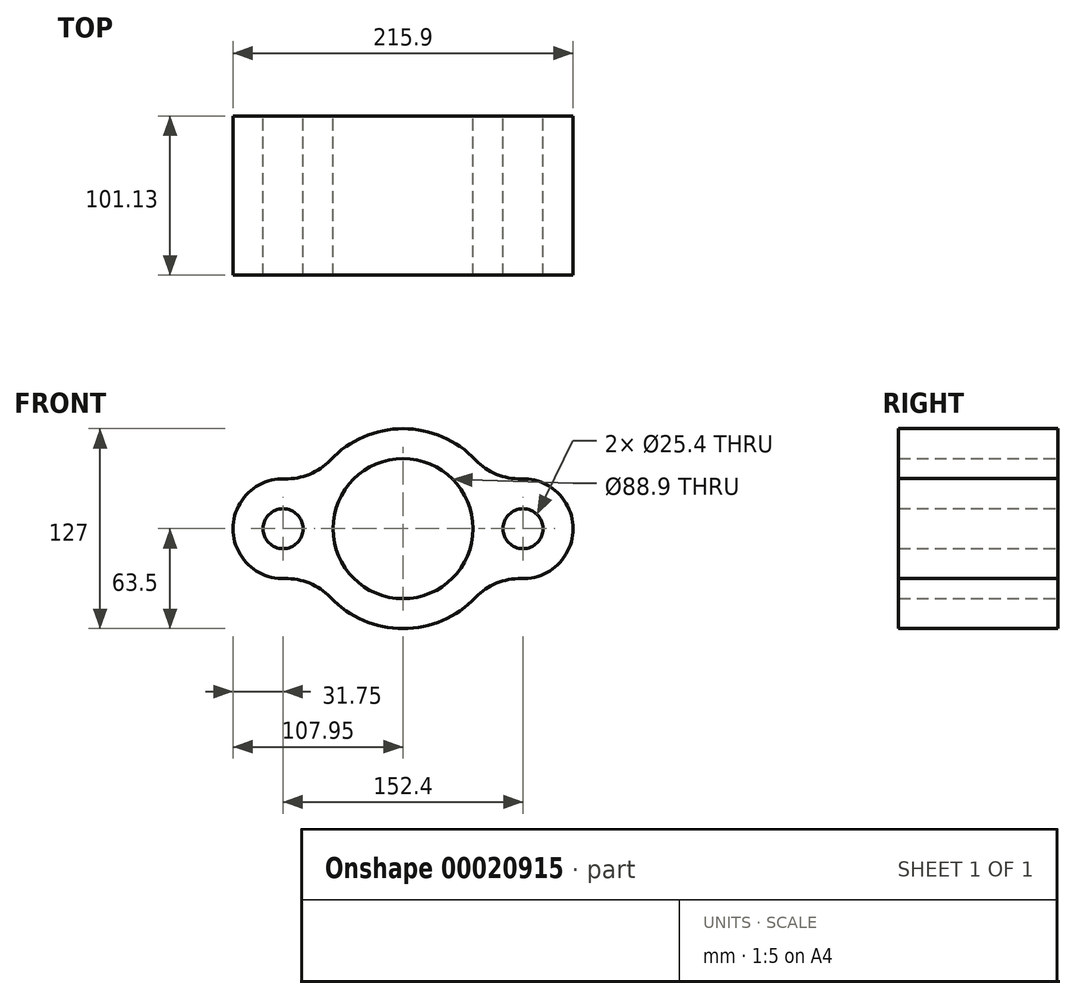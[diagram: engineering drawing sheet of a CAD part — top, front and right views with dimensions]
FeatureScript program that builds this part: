
annotation { "Feature Type Name" : "Feature", "Feature Type Description" : "" }
export const myFeature = defineFeature(function(context is Context, id is Id, definition is map)
    precondition{}
    {
        {
            var Q0;
            Q0=qCreatedBy(makeId("Front.planeOp"),FACE);
            var sketch = newSketch(context, id + "F0", { "sketchPlane" : qUnion([Q0])});
            skCircle(sketch, "E0", {"center": v(0, 0) * mm, "radius": 44.45 * mm});
            skCircle(sketch, "E1", {"center": v(-76.2, 0) * mm, "radius": 12.7 * mm});
            skCircle(sketch, "E2", {"center": v(76.2, 0) * mm, "radius": 12.7 * mm});
            skArc(sketch, "E3", {"start": v(46.14, 43.63) * mm, "mid": v(0, 63.5) * mm, "end": v(-46.14, 43.63) * mm});
            skArc(sketch, "E4", {"start": v(-75.12, 31.73) * mm, "mid": v(-107.95, 0) * mm, "end": v(-75.12, -31.73) * mm});
            skArc(sketch, "E5", {"start": v(75.12, -31.73) * mm, "mid": v(107.95, 0) * mm, "end": v(75.12, 31.73) * mm});
            skArc(sketch, "E6", {"start": v(-75.12, 31.73) * mm, "mid": v(-59.35, 34.56) * mm, "end": v(-46.14, 43.63) * mm});
            skArc(sketch, "E7", {"start": v(-46.14, -43.63) * mm, "mid": v(-59.35, -34.56) * mm, "end": v(-75.12, -31.73) * mm});
            skArc(sketch, "E8", {"start": v(75.12, -31.73) * mm, "mid": v(59.35, -34.56) * mm, "end": v(46.14, -43.63) * mm});
            skArc(sketch, "E9", {"start": v(46.14, 43.63) * mm, "mid": v(59.35, 34.56) * mm, "end": v(75.12, 31.73) * mm});
            skArc(sketch, "E10.trimOffspring", {"start": v(-46.14, -43.63) * mm, "mid": v(0, -63.5) * mm, "end": v(46.14, -43.63) * mm});
            skSolve(sketch);
        }
        {
            var Q0;
            Q0 = qSketchRegion(id + "F0", true);
            var Q1;
            Q1=makeQuery(id+"F0.imprint","IMPRINT",FACE,{"disambiguationData":[TD([[makeQuery(id+"F0.imprint","IMPRINT",EDGE,{"derivedFrom":sQuery(id+"F0.wireOp",EDGE,"E0")}),-1.0]])]});
            extrude(context, id + "F1", {"entities" : qUnion([Q0, Q1]), "depth" : 101.13 * mm});
        }
    });
